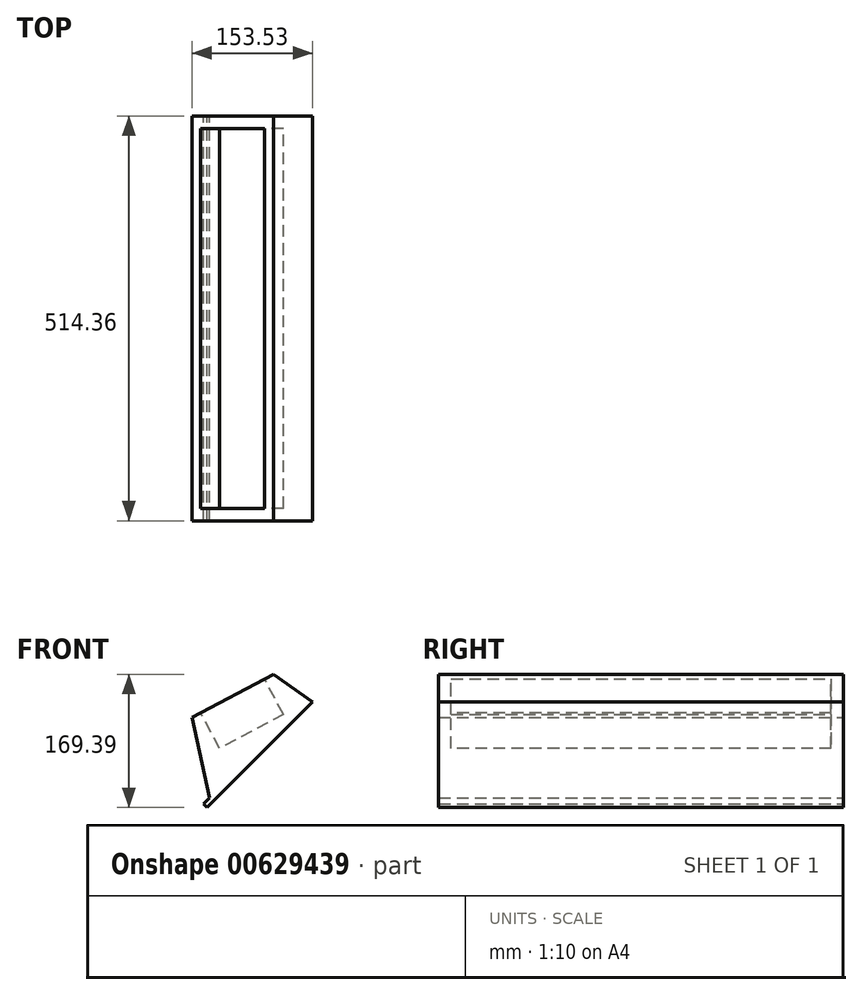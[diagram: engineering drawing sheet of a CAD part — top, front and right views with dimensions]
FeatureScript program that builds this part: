
annotation { "Feature Type Name" : "Feature", "Feature Type Description" : "" }
export const myFeature = defineFeature(function(context is Context, id is Id, definition is map)
    precondition{}
    {
        {
            var Q0;
            Q0=qCreatedBy(makeId("Front.planeOp"),FACE);
            var sketch = newSketch(context, id + "F0", { "sketchPlane" : qUnion([Q0])});
            skLineSegment(sketch, "E0.MirrorCS", {"start": v(35.8, -32.47) * mm, "end": v(31.32, -27.98) * mm});
            skLineSegment(sketch, "E1.MirrorCS", {"start": v(35.8, -32.47) * mm, "end": v(170.19, 101.9) * mm});
            skLineSegment(sketch, "E2.MirrorCS", {"start": v(31.32, -27.98) * mm, "end": v(39.48, -19.82) * mm});
            skLineSegment(sketch, "E3.MirrorCS", {"start": v(16.66, 81.87) * mm, "end": v(120.18, 136.92) * mm});
            skLineSegment(sketch, "E4.MirrorCS", {"start": v(16.66, 81.87) * mm, "end": v(39.48, -19.82) * mm});
            skLineSegment(sketch, "E5.MirrorCS", {"start": v(170.19, 101.9) * mm, "end": v(120.18, 136.92) * mm});
            skSolve(sketch);
        }
        {
            var Q0;
            Q0=makeQuery(id+"F0.imprint","IMPRINT",FACE,{"disambiguationData":[TD([[makeQuery(id+"F0.imprint","IMPRINT",EDGE,{"derivedFrom":sQuery(id+"F0.wireOp",EDGE,"E0.MirrorCS")}),-1.0]])]});
            extrude(context, id + "F1", {"entities" : qUnion([Q0]), "depth" : 508 * mm, "offsetDistance" : 25.4 * mm});
        }
        {
            var Q0;
            Q0=makeQuery(id+"F1.opExtrude","SWEPT_FACE",FACE,{"disambiguationData":[OSD([sQuery(id+"F0.wireOp",EDGE,"E1.MirrorCS")])]});
            var sketch = newSketch(context, id + "F2", { "sketchPlane" : qUnion([Q0])});
            skCircle(sketch, "E6", {"center": v(38.4, 486.69) * mm, "radius": 3.18 * mm});
            skPoint(sketch, "E7.orphan", {"position": v(2.36, 477.16) * mm});
            skPoint(sketch, "E8.start.orphan", {"position": v(34.06, 477.16) * mm});
            skLineSegment(sketch, "E9", {"start": v(38.4, 486.69) * mm, "end": v(74.47, 486.69) * mm, "construction": true});
            skLineSegment(sketch, "E10", {"start": v(74.47, 486.69) * mm, "end": v(74.47, 9.66) * mm, "construction": true});
            skSolve(sketch);
        }
        {
            var Q0;
            Q0=makeQuery(id+"F1.opExtrude","SWEPT_FACE",FACE,{"disambiguationData":[OSD([sQuery(id+"F0.wireOp",EDGE,"E3.MirrorCS")])]});
            var sketch = newSketch(context, id + "F3", { "sketchPlane" : qUnion([Q0])});
            skLineSegment(sketch, "E11.0", {"start": v(157.7, -12.7) * mm, "end": v(65.85, -12.7) * mm});
            skLineSegment(sketch, "E11.1", {"start": v(157.7, -495.3) * mm, "end": v(157.7, -12.7) * mm});
            skLineSegment(sketch, "E11.2", {"start": v(65.85, -495.3) * mm, "end": v(157.7, -495.3) * mm});
            skLineSegment(sketch, "E11.3", {"start": v(65.85, -12.7) * mm, "end": v(65.85, -495.3) * mm});
            skSolve(sketch);
        }
        {
            var Q0;
            Q0 = qSketchRegion(id + "F3", true);
            extrude(context, id + "F4", {"entities" : qUnion([Q0]), "operationType" : NewBodyOperationType.REMOVE, "oppositeDirection" : true, "depth" : 50.8 * mm, "offsetDistance" : 25.4 * mm});
        }
        {
            var Q0;
            Q0=makeQuery(id+"F2.imprint","IMPRINT",FACE,{"disambiguationData":[TD([[makeQuery(id+"F2.imprint","IMPRINT",EDGE,{"derivedFrom":sQuery(id+"F2.wireOp",EDGE,"E6")}),1.0]])]});
            extrude(context, id + "F5", {"entities" : qUnion([Q0]), "operationType" : NewBodyOperationType.REMOVE, "oppositeDirection" : true, "depth" : 12.7 * mm, "offsetDistance" : 25.4 * mm});
        }
        {
            var Q0;
            Q0=makeQuery(id+"F1.opExtrude","CAP_FACE",FACE,{"disambiguationData":[OSD([sQuery(id+"F0.wireOp",EDGE,"E0.MirrorCS"),sQuery(id+"F0.wireOp",EDGE,"E1.MirrorCS"),sQuery(id+"F0.wireOp",EDGE,"E2.MirrorCS"),sQuery(id+"F0.wireOp",EDGE,"E3.MirrorCS"),sQuery(id+"F0.wireOp",EDGE,"E4.MirrorCS"),sQuery(id+"F0.wireOp",EDGE,"E5.MirrorCS")])],"isStart":false});
            extrude(context, id + "F6", {"entities" : qUnion([Q0]), "operationType" : NewBodyOperationType.ADD, "depth" : 3.17 * mm, "offsetDistance" : 25.4 * mm});
        }
        {
            var Q0;
            Q0=makeQuery(id+"F1.opExtrude","CAP_FACE",FACE,{"disambiguationData":[OSD([sQuery(id+"F0.wireOp",EDGE,"E0.MirrorCS"),sQuery(id+"F0.wireOp",EDGE,"E1.MirrorCS"),sQuery(id+"F0.wireOp",EDGE,"E2.MirrorCS"),sQuery(id+"F0.wireOp",EDGE,"E3.MirrorCS"),sQuery(id+"F0.wireOp",EDGE,"E4.MirrorCS"),sQuery(id+"F0.wireOp",EDGE,"E5.MirrorCS")])],"isStart":true});
            extrude(context, id + "F7", {"entities" : qUnion([Q0]), "operationType" : NewBodyOperationType.ADD, "depth" : 3.17 * mm, "offsetDistance" : 25.4 * mm});
        }
    });
